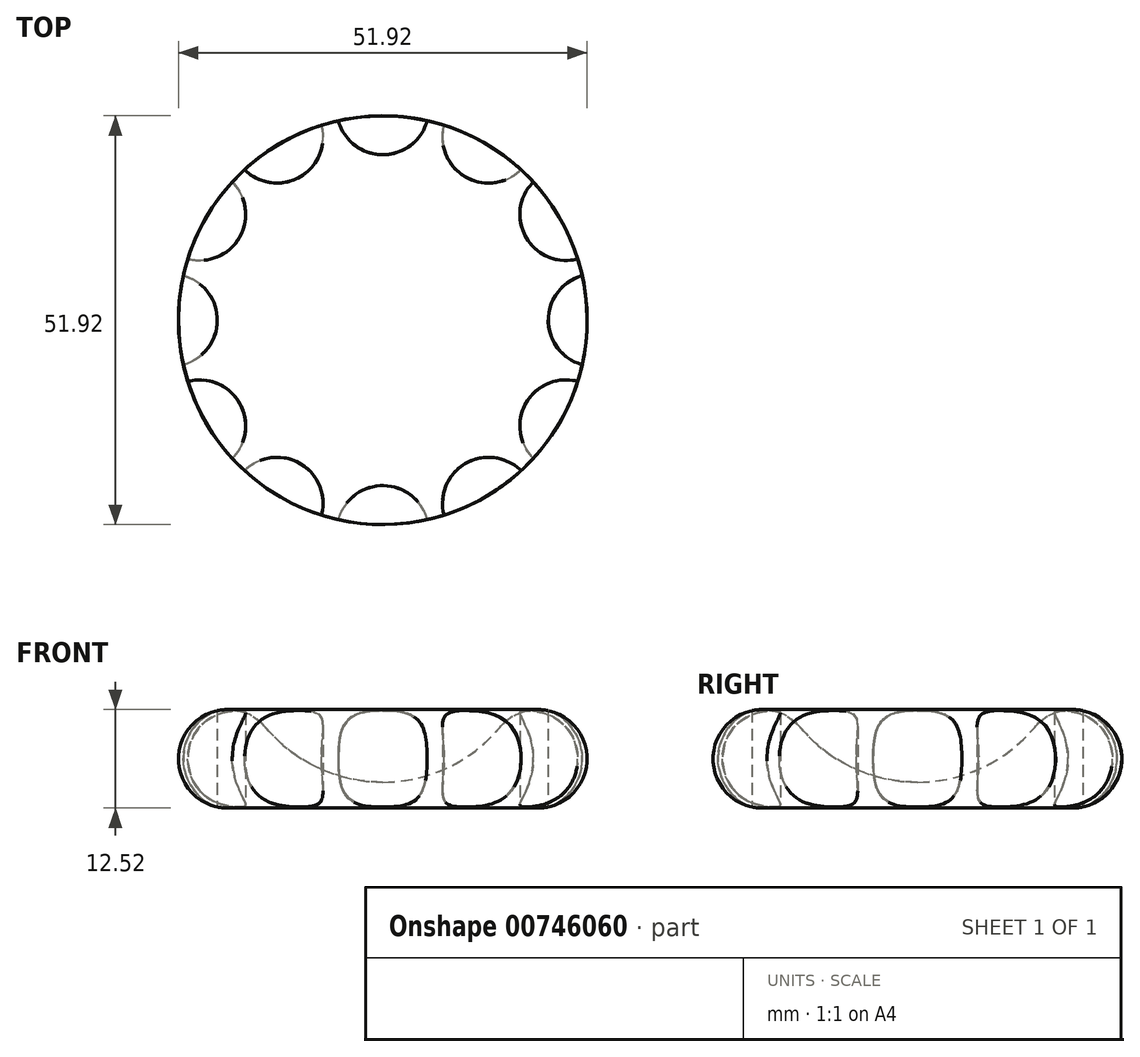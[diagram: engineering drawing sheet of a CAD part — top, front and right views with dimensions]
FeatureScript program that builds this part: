
annotation { "Feature Type Name" : "Feature", "Feature Type Description" : "" }
export const myFeature = defineFeature(function(context is Context, id is Id, definition is map)
    precondition{}
    {
        {
            var Q0;
            Q0=qCreatedBy(makeId("Front.planeOp"),FACE);
            var sketch = newSketch(context, id + "F0", { "sketchPlane" : qUnion([Q0])});
            skArc(sketch, "E0", {"start": v(-14.9, 10.26) * mm, "mid": v(-25.37, 8.91) * mm, "end": v(-19.7, 0) * mm});
            skArc(sketch, "E1", {"start": v(-14.9, 10.26) * mm, "mid": v(-8.22, 5.12) * mm, "end": v(0, 3.29) * mm});
            skLineSegment(sketch, "E2", {"start": v(-19.7, 0) * mm, "end": v(0, 0) * mm});
            skLineSegment(sketch, "E3", {"start": v(0, 3.29) * mm, "end": v(0, 0) * mm});
            skPoint(sketch, "E4.orphan", {"position": v(-35.93, 0) * mm});
            skSolve(sketch);
        }
        {
            var Q0;
            Q0=makeQuery(id+"F0.imprint","IMPRINT",FACE,{"disambiguationData":[TD([[makeQuery(id+"F0.imprint","IMPRINT",EDGE,{"derivedFrom":sQuery(id+"F0.wireOp",EDGE,"E0")}),1.0]])]});
            var Q1;
            Q1 = qSketchRegion(id + "F2", true);
            var Q2;
            Q2=sQuery(id+"F0.wireOp",EDGE,"E3");
            revolve(context, id + "F1", {"surfaceOperationType" : NewSurfaceOperationType.NEW, "entities" : qUnion([Q0, Q1]), "axis" : qUnion([Q2]), "revolveType" : RevolveType.FULL});
        }
        {
            var Q0;
            Q0=qCreatedBy(makeId("Top.planeOp"),FACE);
            var sketch = newSketch(context, id + "F2", { "sketchPlane" : qUnion([Q0])});
            skCircle(sketch, "E5", {"center": v(0, 26.86) * mm, "radius": 5.85 * mm});
            skCircle(sketch, "E6.1.0", {"center": v(-13.43, 23.26) * mm, "radius": 5.85 * mm});
            skCircle(sketch, "E6.2.0", {"center": v(-23.26, 13.43) * mm, "radius": 5.85 * mm});
            skCircle(sketch, "E6.3.0", {"center": v(-26.86, 0) * mm, "radius": 5.85 * mm});
            skCircle(sketch, "E6.4.0", {"center": v(-23.26, -13.43) * mm, "radius": 5.85 * mm});
            skCircle(sketch, "E6.5.0", {"center": v(-13.43, -23.26) * mm, "radius": 5.85 * mm});
            skPoint(sketch, "E6.center", {"position": v(0, 0) * mm});
            skCircle(sketch, "E7.1.6.0", {"center": v(0, -26.86) * mm, "radius": 5.85 * mm});
            skCircle(sketch, "E7.1.7.0", {"center": v(13.43, -23.26) * mm, "radius": 5.85 * mm});
            skCircle(sketch, "E7.1.8.0", {"center": v(23.26, -13.43) * mm, "radius": 5.85 * mm});
            skCircle(sketch, "E7.1.9.0", {"center": v(26.86, 0) * mm, "radius": 5.85 * mm});
            skCircle(sketch, "E7.1.10.0", {"center": v(23.26, 13.43) * mm, "radius": 5.85 * mm});
            skCircle(sketch, "E7.1.11.0", {"center": v(13.43, 23.26) * mm, "radius": 5.85 * mm});
            skSolve(sketch);
        }
        {
            var Q0;
            Q0=makeQuery(id+"F2.imprint","IMPRINT",FACE,{"disambiguationData":[TD([[makeQuery(id+"F2.imprint","IMPRINT",EDGE,{"derivedFrom":sQuery(id+"F2.wireOp",EDGE,"E6.1.0")}),1.0]])]});
            var Q1;
            Q1=makeQuery(id+"F2.imprint","IMPRINT",FACE,{"disambiguationData":[TD([[makeQuery(id+"F2.imprint","IMPRINT",EDGE,{"derivedFrom":sQuery(id+"F2.wireOp",EDGE,"E5")}),1.0]])]});
            var Q2;
            Q2=makeQuery(id+"F2.imprint","IMPRINT",FACE,{"disambiguationData":[TD([[makeQuery(id+"F2.imprint","IMPRINT",EDGE,{"derivedFrom":sQuery(id+"F2.wireOp",EDGE,"E6.11.0")}),1.0]])]});
            var Q3;
            Q3=makeQuery(id+"F2.imprint","IMPRINT",FACE,{"disambiguationData":[TD([[makeQuery(id+"F2.imprint","IMPRINT",EDGE,{"derivedFrom":sQuery(id+"F2.wireOp",EDGE,"E6.10.0")}),1.0]])]});
            var Q4;
            Q4=makeQuery(id+"F2.imprint","IMPRINT",FACE,{"disambiguationData":[TD([[makeQuery(id+"F2.imprint","IMPRINT",EDGE,{"derivedFrom":sQuery(id+"F2.wireOp",EDGE,"E6.9.0")}),1.0]])]});
            var Q5;
            Q5=makeQuery(id+"F2.imprint","IMPRINT",FACE,{"disambiguationData":[TD([[makeQuery(id+"F2.imprint","IMPRINT",EDGE,{"derivedFrom":sQuery(id+"F2.wireOp",EDGE,"E6.8.0")}),1.0]])]});
            var Q6;
            Q6=makeQuery(id+"F2.imprint","IMPRINT",FACE,{"disambiguationData":[TD([[makeQuery(id+"F2.imprint","IMPRINT",EDGE,{"derivedFrom":sQuery(id+"F2.wireOp",EDGE,"E6.7.0")}),1.0]])]});
            var Q7;
            Q7=makeQuery(id+"F2.imprint","IMPRINT",FACE,{"disambiguationData":[TD([[makeQuery(id+"F2.imprint","IMPRINT",EDGE,{"derivedFrom":sQuery(id+"F2.wireOp",EDGE,"E6.6.0")}),1.0]])]});
            var Q8;
            Q8=makeQuery(id+"F2.imprint","IMPRINT",FACE,{"disambiguationData":[TD([[makeQuery(id+"F2.imprint","IMPRINT",EDGE,{"derivedFrom":sQuery(id+"F2.wireOp",EDGE,"E6.5.0")}),1.0]])]});
            var Q9;
            Q9=makeQuery(id+"F2.imprint","IMPRINT",FACE,{"disambiguationData":[TD([[makeQuery(id+"F2.imprint","IMPRINT",EDGE,{"derivedFrom":sQuery(id+"F2.wireOp",EDGE,"E6.4.0")}),1.0]])]});
            var Q10;
            Q10=makeQuery(id+"F2.imprint","IMPRINT",FACE,{"disambiguationData":[TD([[makeQuery(id+"F2.imprint","IMPRINT",EDGE,{"derivedFrom":sQuery(id+"F2.wireOp",EDGE,"E6.3.0")}),1.0]])]});
            var Q11;
            Q11=makeQuery(id+"F2.imprint","IMPRINT",FACE,{"disambiguationData":[TD([[makeQuery(id+"F2.imprint","IMPRINT",EDGE,{"derivedFrom":sQuery(id+"F2.wireOp",EDGE,"E6.2.0")}),1.0]])]});
            var Q12;
            Q12=sQuery(id+"F2.wireOp",EDGE,"E5");
            extrude(context, id + "F3", {"entities" : qUnion([Q0, Q1, Q2, Q3, Q4, Q5, Q6, Q7, Q8, Q9, Q10, Q11]), "operationType" : NewBodyOperationType.REMOVE, "surfaceEntities" : qUnion([Q12]), "depth" : 20.57 * mm, "offsetDistance" : 25.4 * mm});
        }
        {
            var Q0;
            Q0=makeQuery(id+"F1.opRevolve","SWEPT_BODY",BODY,{"disambiguationData":[OSD([sQuery(id+"F0.wireOp",EDGE,"E0"),sQuery(id+"F0.wireOp",EDGE,"E1"),sQuery(id+"F0.wireOp",EDGE,"E2"),sQuery(id+"F0.wireOp",EDGE,"E3")])]});
            var Q1;
            Q1=makeQuery(id+"F1.opRevolve","SWEPT_EDGE",EDGE,{"disambiguationData":[OSD([sQuery(id+"F0.wireOp",EDGE,"E0"),sQuery(id+"F0.wireOp",EDGE,"E1")])]});
            circularPattern(context, id + "F4", {"entities" : qUnion([Q0]), "axis" : qUnion([Q1]), "angle" : 360 * degree, "instanceCount" : 12, "equalSpace" : true});
        }
    });
